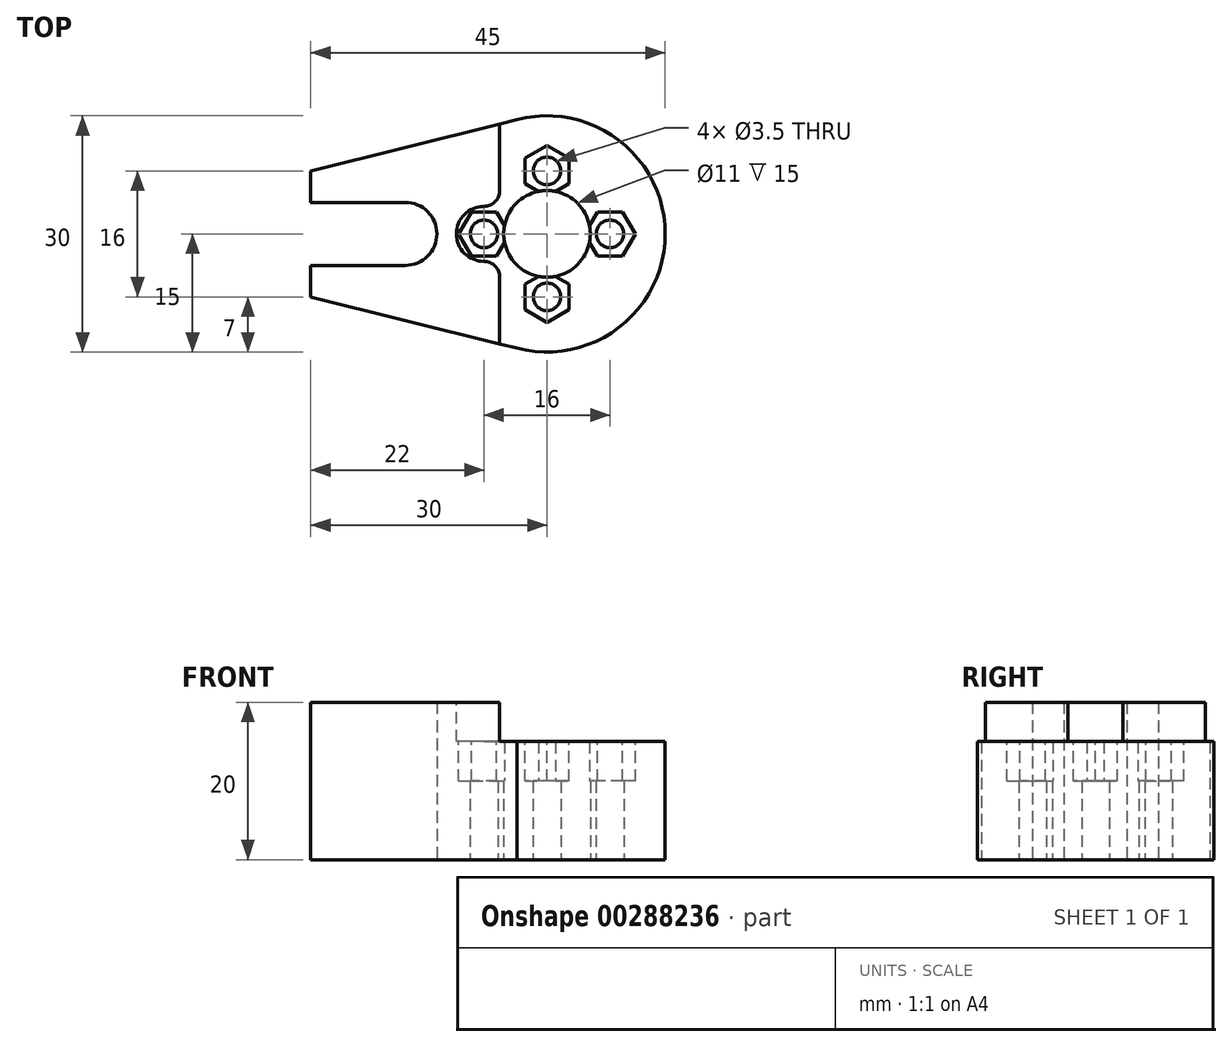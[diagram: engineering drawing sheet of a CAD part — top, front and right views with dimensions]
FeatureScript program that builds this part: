
annotation { "Feature Type Name" : "Feature", "Feature Type Description" : "" }
export const myFeature = defineFeature(function(context is Context, id is Id, definition is map)
    precondition{}
    {
        {
            var Q0;
            Q0=qCreatedBy(makeId("Top.planeOp"),FACE);
            var sketch = newSketch(context, id + "F0", { "sketchPlane" : qUnion([Q0])});
            skCircle(sketch, "E0", {"center": v(0, 0) * mm, "radius": 5.5 * mm});
            skArc(sketch, "E1", {"start": v(-18, -4) * mm, "mid": v(-14, 0) * mm, "end": v(-18, 4) * mm});
            skArc(sketch, "E2", {"start": v(-3.84, -14.5) * mm, "mid": v(15, 0) * mm, "end": v(-3.84, 14.5) * mm});
            skLineSegment(sketch, "E3", {"start": v(-3.84, 14.5) * mm, "end": v(-30, 8) * mm});
            skLineSegment(sketch, "E4", {"start": v(-30, 8) * mm, "end": v(-30, 4) * mm});
            skLineSegment(sketch, "E5", {"start": v(-18, 4) * mm, "end": v(-30, 4) * mm});
            skLineSegment(sketch, "E6.MirrorCS", {"start": v(-18, -4) * mm, "end": v(-30, -4) * mm});
            skLineSegment(sketch, "E7.MirrorCS", {"start": v(-3.84, -14.5) * mm, "end": v(-30, -8) * mm});
            skLineSegment(sketch, "E8.MirrorCS", {"start": v(-30, -8) * mm, "end": v(-30, -4) * mm});
            skSolve(sketch);
        }
        {
            var Q0;
            Q0=makeQuery(id+"F0.imprint","IMPRINT",FACE,{"disambiguationData":[TD([[makeQuery(id+"F0.imprint","IMPRINT",EDGE,{"derivedFrom":sQuery(id+"F0.wireOp",EDGE,"E0")}),-1.0]])]});
            extrude(context, id + "F1", {"entities" : qUnion([Q0]), "depth" : 20 * mm});
        }
        {
            var Q0;
            Q0=makeQuery(id+"F1.opExtrude","CAP_FACE",FACE,{"disambiguationData":[OSD([sQuery(id+"F0.wireOp",EDGE,"E0"),sQuery(id+"F0.wireOp",EDGE,"E1"),sQuery(id+"F0.wireOp",EDGE,"E2"),sQuery(id+"F0.wireOp",EDGE,"E3"),sQuery(id+"F0.wireOp",EDGE,"E4"),sQuery(id+"F0.wireOp",EDGE,"E5"),sQuery(id+"F0.wireOp",EDGE,"E6.MirrorCS"),sQuery(id+"F0.wireOp",EDGE,"E7.MirrorCS"),sQuery(id+"F0.wireOp",EDGE,"E8.MirrorCS")])],"isStart":false});
            var sketch = newSketch(context, id + "F2", { "sketchPlane" : qUnion([Q0])});
            skPoint(sketch, "E9", {"position": v(0, 8) * mm});
            skPoint(sketch, "E10.1.0", {"position": v(-8, 0) * mm});
            skPoint(sketch, "E10.2.0", {"position": v(0, -8) * mm});
            skPoint(sketch, "E10.3.0", {"position": v(8, 0) * mm});
            skPoint(sketch, "E10.center", {"position": v(0, 0) * mm});
            skSolve(sketch);
        }
        {
            var Q0;
            Q0=sQuery(id+"F2.wireOp",VERTEX,"E10.3.0");
            var Q1;
            Q1=sQuery(id+"F2.wireOp",VERTEX,"E10.2.0");
            var Q2;
            Q2=sQuery(id+"F2.wireOp",VERTEX,"E10.1.0");
            var Q3;
            Q3=sQuery(id+"F2.wireOp",VERTEX,"E9");
            var Q4;
            Q4=makeQuery(id+"F1.opExtrude","SWEPT_BODY",BODY,{"disambiguationData":[OSD([sQuery(id+"F0.wireOp",EDGE,"E0"),sQuery(id+"F0.wireOp",EDGE,"E1"),sQuery(id+"F0.wireOp",EDGE,"E2"),sQuery(id+"F0.wireOp",EDGE,"E3"),sQuery(id+"F0.wireOp",EDGE,"E4"),sQuery(id+"F0.wireOp",EDGE,"E5"),sQuery(id+"F0.wireOp",EDGE,"E6.MirrorCS"),sQuery(id+"F0.wireOp",EDGE,"E7.MirrorCS"),sQuery(id+"F0.wireOp",EDGE,"E8.MirrorCS")])]});
            hole(context, id + "F3", {"style" : HoleStyle.SIMPLE, "endStyle" : HoleEndStyle.THROUGH, "holeDiameter" : 3.5 * mm, "tappedDepth" : 12 * mm, "tapClearance" : 3, "startFromSketch" : true, "locations" : qUnion([Q0, Q1, Q2, Q3]), "scope" : qUnion([Q4])});
        }
        {
            var Q0;
            Q0=makeQuery(id+"F1.opExtrude","CAP_FACE",FACE,{"disambiguationData":[OSD([sQuery(id+"F0.wireOp",EDGE,"E0"),sQuery(id+"F0.wireOp",EDGE,"E1"),sQuery(id+"F0.wireOp",EDGE,"E2"),sQuery(id+"F0.wireOp",EDGE,"E3"),sQuery(id+"F0.wireOp",EDGE,"E4"),sQuery(id+"F0.wireOp",EDGE,"E5"),sQuery(id+"F0.wireOp",EDGE,"E6.MirrorCS"),sQuery(id+"F0.wireOp",EDGE,"E7.MirrorCS"),sQuery(id+"F0.wireOp",EDGE,"E8.MirrorCS")])],"isStart":false});
            var sketch = newSketch(context, id + "F4", { "sketchPlane" : qUnion([Q0])});
            skCircle(sketch, "E11.cCircle", {"center": v(8, 0) * mm, "radius": 2.8 * mm, "construction": true});
            skLineSegment(sketch, "E11.0", {"start": v(9.62, 2.8) * mm, "end": v(11.23, 0) * mm});
            skLineSegment(sketch, "E11.1", {"start": v(11.23, 0) * mm, "end": v(9.62, -2.8) * mm});
            skLineSegment(sketch, "E11.2", {"start": v(9.62, -2.8) * mm, "end": v(6.38, -2.8) * mm});
            skLineSegment(sketch, "E11.3", {"start": v(6.38, -2.8) * mm, "end": v(4.77, 0) * mm});
            skLineSegment(sketch, "E11.4", {"start": v(4.77, 0) * mm, "end": v(6.38, 2.8) * mm});
            skLineSegment(sketch, "E11.5", {"start": v(6.38, 2.8) * mm, "end": v(9.62, 2.8) * mm});
            skPoint(sketch, "E11.0.midPoint", {"position": v(10.42, 1.4) * mm});
            skLineSegment(sketch, "E12.1.0", {"start": v(-2.8, 6.38) * mm, "end": v(-2.8, 9.62) * mm});
            skPoint(sketch, "E12.1.1", {"position": v(-1.4, 10.42) * mm});
            skCircle(sketch, "E12.1.2", {"center": v(0, 8) * mm, "radius": 2.8 * mm, "construction": true});
            skLineSegment(sketch, "E12.1.3", {"start": v(0, 11.23) * mm, "end": v(2.8, 9.62) * mm});
            skLineSegment(sketch, "E12.1.4", {"start": v(2.8, 6.38) * mm, "end": v(0, 4.77) * mm});
            skLineSegment(sketch, "E12.1.5", {"start": v(-2.8, 9.62) * mm, "end": v(0, 11.23) * mm});
            skLineSegment(sketch, "E12.1.6", {"start": v(2.8, 9.62) * mm, "end": v(2.8, 6.38) * mm});
            skLineSegment(sketch, "E12.1.7", {"start": v(0, 4.77) * mm, "end": v(-2.8, 6.38) * mm});
            skLineSegment(sketch, "E12.2.0", {"start": v(-6.38, -2.8) * mm, "end": v(-9.62, -2.8) * mm});
            skPoint(sketch, "E12.2.1", {"position": v(-10.42, -1.4) * mm});
            skCircle(sketch, "E12.2.2", {"center": v(-8, 0) * mm, "radius": 2.8 * mm, "construction": true});
            skLineSegment(sketch, "E12.2.3", {"start": v(-11.23, 0) * mm, "end": v(-9.62, 2.8) * mm});
            skLineSegment(sketch, "E12.2.4", {"start": v(-6.38, 2.8) * mm, "end": v(-4.77, 0) * mm});
            skLineSegment(sketch, "E12.2.5", {"start": v(-9.62, -2.8) * mm, "end": v(-11.23, 0) * mm});
            skLineSegment(sketch, "E12.2.6", {"start": v(-9.62, 2.8) * mm, "end": v(-6.38, 2.8) * mm});
            skLineSegment(sketch, "E12.2.7", {"start": v(-4.77, 0) * mm, "end": v(-6.38, -2.8) * mm});
            skLineSegment(sketch, "E12.3.0", {"start": v(2.8, -6.38) * mm, "end": v(2.8, -9.62) * mm});
            skPoint(sketch, "E12.3.1", {"position": v(1.4, -10.42) * mm});
            skCircle(sketch, "E12.3.2", {"center": v(0, -8) * mm, "radius": 2.8 * mm, "construction": true});
            skLineSegment(sketch, "E12.3.3", {"start": v(0, -11.23) * mm, "end": v(-2.8, -9.62) * mm});
            skLineSegment(sketch, "E12.3.4", {"start": v(-2.8, -6.38) * mm, "end": v(0, -4.77) * mm});
            skLineSegment(sketch, "E12.3.5", {"start": v(2.8, -9.62) * mm, "end": v(0, -11.23) * mm});
            skLineSegment(sketch, "E12.3.6", {"start": v(-2.8, -9.62) * mm, "end": v(-2.8, -6.38) * mm});
            skLineSegment(sketch, "E12.3.7", {"start": v(0, -4.77) * mm, "end": v(2.8, -6.38) * mm});
            skPoint(sketch, "E12.center", {"position": v(0, 0) * mm});
            skSolve(sketch);
        }
        {
            var Q0;
            Q0 = qSketchRegion(id + "F4", true);
            extrude(context, id + "F5", {"entities" : qUnion([Q0]), "operationType" : NewBodyOperationType.REMOVE, "oppositeDirection" : true, "depth" : 10 * mm});
        }
        {
            var Q0;
            Q0=makeQuery(id+"F1.opExtrude","CAP_FACE",FACE,{"disambiguationData":[OSD([sQuery(id+"F0.wireOp",EDGE,"E0"),sQuery(id+"F0.wireOp",EDGE,"E1"),sQuery(id+"F0.wireOp",EDGE,"E2"),sQuery(id+"F0.wireOp",EDGE,"E3"),sQuery(id+"F0.wireOp",EDGE,"E4"),sQuery(id+"F0.wireOp",EDGE,"E5"),sQuery(id+"F0.wireOp",EDGE,"E6.MirrorCS"),sQuery(id+"F0.wireOp",EDGE,"E7.MirrorCS"),sQuery(id+"F0.wireOp",EDGE,"E8.MirrorCS")])],"isStart":false});
            var sketch = newSketch(context, id + "F6", { "sketchPlane" : qUnion([Q0])});
            skArc(sketch, "E13.0", {"start": v(-3.84, -14.5) * mm, "mid": v(15, 0) * mm, "end": v(-3.84, 14.5) * mm});
            skLineSegment(sketch, "E14.0", {"start": v(-3.84, -14.5) * mm, "end": v(-6, -13.96) * mm});
            skLineSegment(sketch, "E15.0", {"start": v(-3.84, 14.5) * mm, "end": v(-6, 13.96) * mm});
            skLineSegment(sketch, "E16", {"start": v(-6, 13.96) * mm, "end": v(-6, 3.5) * mm});
            skArc(sketch, "E17", {"start": v(-8, 3.5) * mm, "mid": v(-11.5, 0) * mm, "end": v(-8, -3.5) * mm});
            skLineSegment(sketch, "E18", {"start": v(-8, 3.5) * mm, "end": v(-6, 3.5) * mm});
            skLineSegment(sketch, "E19.trimOffspring", {"start": v(-6, -3.5) * mm, "end": v(-6, -13.96) * mm});
            skLineSegment(sketch, "E20", {"start": v(-6, -3.5) * mm, "end": v(-8, -3.5) * mm});
            skSolve(sketch);
        }
        {
            var Q0;
            Q0 = qSketchRegion(id + "F6", true);
            extrude(context, id + "F7", {"entities" : qUnion([Q0]), "operationType" : NewBodyOperationType.REMOVE, "oppositeDirection" : true, "depth" : 5 * mm});
        }
        {
            var Q0;
            Q0=makeQuery(id+"F7.boolean.opBoolean","COPY",EDGE,{"derivedFrom":makeQuery(id+"F7.opExtrude","CAP_EDGE",EDGE,{"disambiguationData":[OSD([sQuery(id+"F6.wireOp",EDGE,"E19.trimOffspring")])],"isStart":true})});
            var Q1;
            Q1=makeQuery(id+"F7.boolean.opBoolean","COPY",EDGE,{"derivedFrom":makeQuery(id+"F7.opExtrude","CAP_EDGE",EDGE,{"disambiguationData":[OSD([sQuery(id+"F6.wireOp",EDGE,"E16")])],"isStart":true})});
            var Q2;
            Q2=makeQuery(id+"F7.boolean.opBoolean","COPY",EDGE,{"derivedFrom":makeQuery(id+"F7.opExtrude","SWEPT_EDGE",EDGE,{"disambiguationData":[OSD([sQuery(id+"F6.wireOp",EDGE,"E19.trimOffspring"),sQuery(id+"F6.wireOp",EDGE,"E20")])]})});
            var Q3;
            Q3=makeQuery(id+"F7.boolean.opBoolean","COPY",EDGE,{"derivedFrom":makeQuery(id+"F7.opExtrude","SWEPT_EDGE",EDGE,{"disambiguationData":[OSD([sQuery(id+"F6.wireOp",EDGE,"E16"),sQuery(id+"F6.wireOp",EDGE,"E18")])]})});
            fillet(context, id + "F8", {"entities" : qUnion([Q0, Q1, Q2, Q3]), "radius" : 2 * mm, "tangentPropagation" : true, "allowEdgeOverflow" : false});
        }
    });
